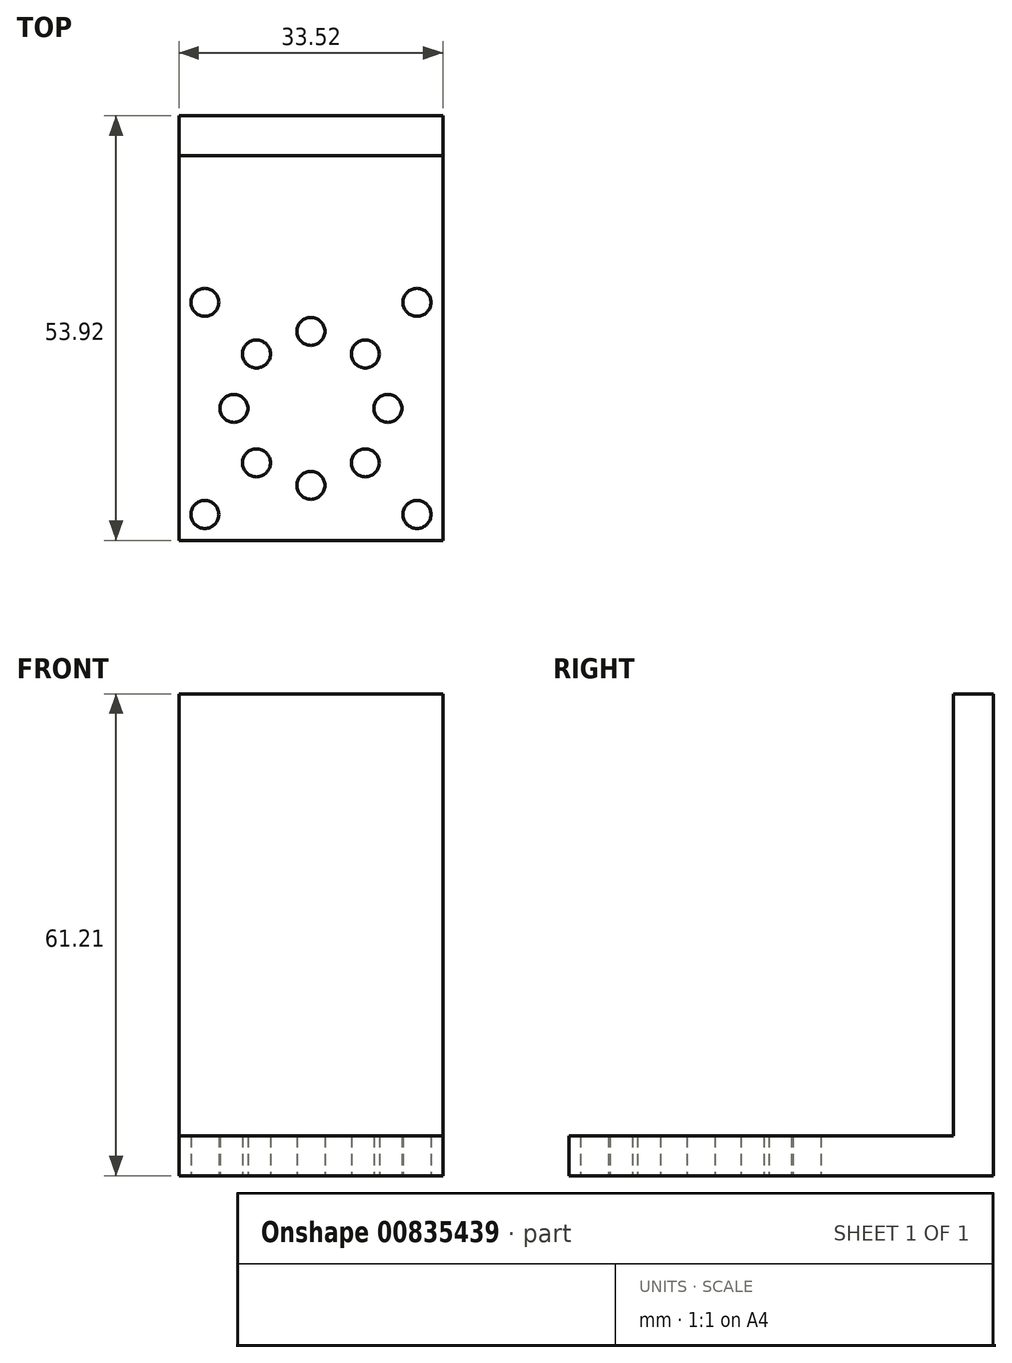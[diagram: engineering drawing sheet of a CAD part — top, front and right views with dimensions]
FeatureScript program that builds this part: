
annotation { "Feature Type Name" : "Feature", "Feature Type Description" : "" }
export const myFeature = defineFeature(function(context is Context, id is Id, definition is map)
    precondition{}
    {
        {
            var Q0;
            Q0=qCreatedBy(makeId("Top.planeOp"),FACE);
            var sketch = newSketch(context, id + "F0", { "sketchPlane" : qUnion([Q0])});
            skLineSegment(sketch, "E0.bottom", {"start": v(16.76, -16.76) * mm, "end": v(-16.76, -16.76) * mm});
            skLineSegment(sketch, "E0.top", {"start": v(16.76, 16.76) * mm, "end": v(-16.76, 16.76) * mm});
            skLineSegment(sketch, "E0.left", {"start": v(16.76, -16.76) * mm, "end": v(16.76, 16.76) * mm});
            skLineSegment(sketch, "E0.right", {"start": v(-16.76, -16.76) * mm, "end": v(-16.76, 16.76) * mm});
            skPoint(sketch, "E0.middle", {"position": v(0, 0) * mm});
            skCircle(sketch, "E1", {"center": v(-13.47, -13.47) * mm, "radius": 1.78 * mm});
            skCircle(sketch, "E2", {"center": v(13.47, -13.47) * mm, "radius": 1.78 * mm});
            skCircle(sketch, "E3", {"center": v(13.47, 13.47) * mm, "radius": 1.78 * mm});
            skCircle(sketch, "E4", {"center": v(-13.47, 13.47) * mm, "radius": 1.78 * mm});
            skLineSegment(sketch, "E5", {"start": v(-13.47, -13.47) * mm, "end": v(13.47, 13.47) * mm, "construction": true});
            skLineSegment(sketch, "E6", {"start": v(13.47, -13.47) * mm, "end": v(-13.47, 13.47) * mm, "construction": true});
            skLineSegment(sketch, "E7", {"start": v(-13.47, 13.47) * mm, "end": v(13.47, 13.47) * mm, "construction": true});
            skLineSegment(sketch, "E8", {"start": v(-13.47, -13.47) * mm, "end": v(-13.47, 13.47) * mm, "construction": true});
            skCircle(sketch, "E9", {"center": v(-9.78, 0) * mm, "radius": 1.78 * mm});
            skCircle(sketch, "E10", {"center": v(0, 9.78) * mm, "radius": 1.78 * mm});
            skCircle(sketch, "E11", {"center": v(9.78, 0) * mm, "radius": 1.78 * mm});
            skCircle(sketch, "E12", {"center": v(0, -9.78) * mm, "radius": 1.78 * mm});
            skCircle(sketch, "E13", {"center": v(-6.91, 6.91) * mm, "radius": 1.78 * mm});
            skCircle(sketch, "E14", {"center": v(-6.91, -6.91) * mm, "radius": 1.78 * mm});
            skCircle(sketch, "E15", {"center": v(6.91, -6.91) * mm, "radius": 1.78 * mm});
            skCircle(sketch, "E16", {"center": v(6.91, 6.91) * mm, "radius": 1.78 * mm});
            skLineSegment(sketch, "E17", {"start": v(0, 0) * mm, "end": v(6.91, -6.91) * mm, "construction": true});
            skLineSegment(sketch, "E18", {"start": v(0, 0) * mm, "end": v(6.91, 6.91) * mm, "construction": true});
            skLineSegment(sketch, "E19", {"start": v(-9.78, 0) * mm, "end": v(0, 0) * mm, "construction": true});
            skLineSegment(sketch, "E20", {"start": v(-13.47, 13.47) * mm, "end": v(-13.47, 16.76) * mm, "construction": true});
            skLineSegment(sketch, "E21", {"start": v(9.78, 0) * mm, "end": v(9.78, 1.78) * mm, "construction": true});
            skLineSegment(sketch, "E22", {"start": v(-13.47, -13.47) * mm, "end": v(13.47, -13.47) * mm, "construction": true});
            skSolve(sketch);
        }
        {
            var Q0;
            Q0=qCreatedBy(makeId("Top.planeOp"),FACE);
            var sketch = newSketch(context, id + "F1", { "sketchPlane" : qUnion([Q0])});
            skLineSegment(sketch, "E23.bottom", {"start": v(-16.76, -16.76) * mm, "end": v(16.76, -16.76) * mm});
            skLineSegment(sketch, "E23.top", {"start": v(-16.76, 39.37) * mm, "end": v(16.76, 39.37) * mm});
            skLineSegment(sketch, "E23.left", {"start": v(-16.76, -16.76) * mm, "end": v(-16.76, 39.37) * mm});
            skLineSegment(sketch, "E23.right", {"start": v(16.76, -16.76) * mm, "end": v(16.76, 39.37) * mm});
            skLineSegment(sketch, "E24", {"start": v(0, 0) * mm, "end": v(0, 39.37) * mm, "construction": true});
            skLineSegment(sketch, "E25.top", {"start": v(-16.76, 44.45) * mm, "end": v(16.76, 44.45) * mm});
            skLineSegment(sketch, "E25.left", {"start": v(-16.76, 39.37) * mm, "end": v(-16.76, 44.45) * mm});
            skLineSegment(sketch, "E25.right", {"start": v(16.76, 39.37) * mm, "end": v(16.76, 44.45) * mm});
            skLineSegment(sketch, "E26.top", {"start": v(-16.76, 16.76) * mm, "end": v(16.76, 16.76) * mm});
            skLineSegment(sketch, "E26.left", {"start": v(-16.76, -16.76) * mm, "end": v(-16.76, 16.76) * mm});
            skLineSegment(sketch, "E26.right", {"start": v(16.76, -16.76) * mm, "end": v(16.76, 16.76) * mm});
            skSolve(sketch);
        }
        {
            var Q0;
            Q0=qSketchRegion(id+"F0",true);
            extrude(context, id + "F2", {"entities" : qUnion([Q0]), "depth" : 5.08 * mm, "offsetDistance" : 25.4 * mm});
        }
        {
            var Q0;
            Q0=makeQuery(id+"F1.imprint","IMPRINT",FACE,{"disambiguationData":[TD([[makeQuery(id+"F1.imprint","IMPRINT",EDGE,{"derivedFrom":sQuery(id+"F1.wireOp",EDGE,"E23.left")}),-1.0]])]});
            var Q1;
            Q1=makeQuery(id+"F1.imprint","IMPRINT",FACE,{"disambiguationData":[TD([[makeQuery(id+"F1.imprint","IMPRINT",EDGE,{"derivedFrom":sQuery(id+"F1.wireOp",EDGE,"E23.top")}),1.0]])]});
            extrude(context, id + "F3", {"entities" : qUnion([Q0, Q1]), "operationType" : NewBodyOperationType.ADD, "depth" : 5.08 * mm, "offsetDistance" : 25.4 * mm});
        }
        {
            var Q0;
            Q0=makeQuery(id+"F2.opExtrude","SWEPT_BODY",BODY,{"disambiguationData":[OSD([sQuery(id+"F0.wireOp",EDGE,"E0.bottom"),sQuery(id+"F0.wireOp",EDGE,"E0.top"),sQuery(id+"F0.wireOp",EDGE,"E0.left"),sQuery(id+"F0.wireOp",EDGE,"E0.right"),sQuery(id+"F0.wireOp",EDGE,"E1"),sQuery(id+"F0.wireOp",EDGE,"E2"),sQuery(id+"F0.wireOp",EDGE,"E3"),sQuery(id+"F0.wireOp",EDGE,"E4"),sQuery(id+"F0.wireOp",EDGE,"E9"),sQuery(id+"F0.wireOp",EDGE,"E10"),sQuery(id+"F0.wireOp",EDGE,"E11"),sQuery(id+"F0.wireOp",EDGE,"E12"),sQuery(id+"F0.wireOp",EDGE,"E13"),sQuery(id+"F0.wireOp",EDGE,"E14"),sQuery(id+"F0.wireOp",EDGE,"E15"),sQuery(id+"F0.wireOp",EDGE,"E16")])]});
            var Q1;
            Q1=sQuery(id+"F1.wireOp",EDGE,"E25.top");
            transform(context, id + "F4", {"entities" : qUnion([Q0]), "transformType" : TransformType.ROTATION, "transformAxis" : qUnion([Q1]), "angle" : 90 * degree, "oppositeDirection" : true, "makeCopy" : false});
        }
        {
            var Q0;
            Q0=qCreatedBy(makeId("Top.planeOp"),FACE);
            var sketch = newSketch(context, id + "F5", { "sketchPlane" : qUnion([Q0])});
            skLineSegment(sketch, "E27.bottom", {"start": v(-16.76, -16.76) * mm, "end": v(16.76, -16.76) * mm});
            skLineSegment(sketch, "E27.top", {"start": v(-16.76, 37.16) * mm, "end": v(16.76, 37.16) * mm});
            skLineSegment(sketch, "E27.left", {"start": v(-16.76, -16.76) * mm, "end": v(-16.76, 37.16) * mm});
            skLineSegment(sketch, "E27.right", {"start": v(16.76, -16.76) * mm, "end": v(16.76, 37.16) * mm});
            skLineSegment(sketch, "E28.bottom", {"start": v(16.76, 37.16) * mm, "end": v(-16.76, 37.16) * mm});
            skLineSegment(sketch, "E28.top", {"start": v(16.76, 16.76) * mm, "end": v(-16.76, 16.76) * mm});
            skLineSegment(sketch, "E28.left", {"start": v(16.76, 37.16) * mm, "end": v(16.76, 16.76) * mm});
            skLineSegment(sketch, "E28.right", {"start": v(-16.76, 37.16) * mm, "end": v(-16.76, 16.76) * mm});
            skLineSegment(sketch, "E29.top", {"start": v(-16.76, 32.08) * mm, "end": v(16.76, 32.08) * mm});
            skLineSegment(sketch, "E29.left", {"start": v(-16.76, 32.08) * mm, "end": v(-16.76, 37.16) * mm});
            skLineSegment(sketch, "E29.right", {"start": v(16.76, 32.08) * mm, "end": v(16.76, 37.16) * mm});
            skLineSegment(sketch, "E30", {"start": v(0, 0) * mm, "end": v(0, 32.08) * mm, "construction": true});
            skSolve(sketch);
        }
        {
            var Q0;
            Q0=makeQuery(id+"F2.opExtrude","SWEPT_BODY",BODY,{"disambiguationData":[OSD([sQuery(id+"F0.wireOp",EDGE,"E0.bottom"),sQuery(id+"F0.wireOp",EDGE,"E0.top"),sQuery(id+"F0.wireOp",EDGE,"E0.left"),sQuery(id+"F0.wireOp",EDGE,"E0.right"),sQuery(id+"F0.wireOp",EDGE,"E1"),sQuery(id+"F0.wireOp",EDGE,"E2"),sQuery(id+"F0.wireOp",EDGE,"E3"),sQuery(id+"F0.wireOp",EDGE,"E4"),sQuery(id+"F0.wireOp",EDGE,"E9"),sQuery(id+"F0.wireOp",EDGE,"E10"),sQuery(id+"F0.wireOp",EDGE,"E11"),sQuery(id+"F0.wireOp",EDGE,"E12"),sQuery(id+"F0.wireOp",EDGE,"E13"),sQuery(id+"F0.wireOp",EDGE,"E14"),sQuery(id+"F0.wireOp",EDGE,"E15"),sQuery(id+"F0.wireOp",EDGE,"E16")])]});
            var Q1;
            Q1=makeQuery(id+"F3.opExtrude","CAP_VERTEX",VERTEX,{"disambiguationData":[OSD([sQuery(id+"F1.wireOp",EDGE,"E25.top"),sQuery(id+"F1.wireOp",EDGE,"E25.right")])],"isStart":false});
            var Q2;
            Q2=sQuery(id+"F5.wireOp",VERTEX,"E27.top.end");
            transform(context, id + "F6", {"entities" : qUnion([Q0]), "transformType" : TransformType.TRANSLATION_ENTITY, "oppositeDirectionEntity" : false, "transformLine" : qUnion([Q1, Q2]), "makeCopy" : false});
        }
        {
            var Q0;
            Q0=qSketchRegion(id+"F0",true);
            var Q1;
            Q1=makeQuery(id+"F5.imprint","IMPRINT",FACE,{"disambiguationData":[TD([[makeQuery(id+"F5.imprint","IMPRINT",EDGE,{"derivedFrom":sQuery(id+"F5.wireOp",EDGE,"E28.top")}),-1.0]])]});
            extrude(context, id + "F7", {"entities" : qUnion([Q0, Q1]), "operationType" : NewBodyOperationType.ADD, "depth" : 5.08 * mm, "offsetDistance" : 25.4 * mm});
        }
    });
